# Revit family: SIMES_S.5402W_Minilinear-Miniround
name_source: partatom
category: Lighting Fixtures
revit_build: Autodesk Revit 2016 (Build: 20150714_1515(x64)
units: mm (PartAtom-declared; Revit-internal decimal feet)

## family parameters
Cut with Voids When Loaded = No
Host = Face
Light Source = Yes
OmniClass Number = 23.80.70.14
OmniClass Title = Luminaries for External Lighting
Part Type = Normal
Room Calculation Point = No
Round Connector Dimension = Use Diameter
Shared = No

## types (1)
- SIMES_S.5402W_Minilinear-Miniround
    Approval mark = CE
    Assembly Code = D5020
    BIMobject category = Outside
    BIMobject category code = lighting-outside
    BIMobject main category = Lighting
    BIMobject main category code = lighting
    Brand url = http://www.simes.it
    Color Filter = 16777215
    Color Rendering Index = CRI 90
    Colour Temperature = 3000
    Control Gear = electronic transformer
    Default Elevation = 1219 mm
    Description = MINIROUND FULL GLASS
Art. S.5402W
MODULES LED 3000K  230V CRI 90 MacAdam step 3
Rated luminaire luminous flux: 392lm
Rated input power: 10.7W
Luminaire efficacy: 37lm/W
Electronic ballast 220÷240V 50/60Hz
CE

PRODUCT TYPE
Inground walk over fitting. Recessing depth 95 mm. IP rating IP 67
MATERIAL CHARACTERISTICS
"Copper Free" Aluminium die cast housing in EN AB-44100 with high resistance against corrosion. Stone wash surface treatment prior to painting process. A4 grade Stainless Steel screws with 2,5-3% molybdenum content which increases the resistance against corrosion. Pre treated Silicone Gaskets (Minilinear). Painting Process : 3 Step Process
1) Surface treatment with BONDERITE. A heavy metal free chemical surface treatment containing ceramic nano particles giving a cohesive, inorganic and highly dense protective coating. 2) PRE POLYMERIZATION a process of introducing an epoxy primer with excellent characteristics to the paint which also offers very high resistance to oxidation due to its Zinc content. 3) POLYMERIZATION a process with the application of polyester powder with high resistance against UV rays and harsh weather conditions. Resistance test protection for Marine applications for 1200h.  Mechanical resistance IK 09 Maximum load capacity 500 Kg
LIGHTING PERFORMANCE
 acid-etched  Toughened glass 6mm thick. Lamp  fixed position. LOR -- Compact electronic ballast to guarantee better lamp stability, lifetime and reduced energy consumption.
LOW SURFACE TEMPERATURE
Surface temperature of glass 40°C (Ta 25°C) Electronic Ballast generating less heat. 
Specific layout of internal components allow for better heat dissipation therefore limiting the temperature generated inside the fitting.
RECESSING BOX
Recessing box in alluminium (Minilinear) or polypropylene (Miniround)with cable entry on all 4 sides also allows: 1) Easy wiring; 2) Cable management for fast connector; 3) Easy access to the fitting for maintenance purposes.
WIRING
Supply 0.5m cable section type H07RN-F and sealed with B component epoxy resin, wired internally protected by silicon sheaths. Fast connector M20 (Ø 5÷14 mm) supplied as standard for single cable connection . Connector housed inside the recessing box . Connection joint: The housing of Miniround has a 'dove-tail' joint to perfectly connect two or more consecutive fittings  (5 consecutive products create a full circle). Isolation: CLASS I . Finishing : FULL-GLASS Weight: 2.7 Kg Glow Wire test: --
L.E.D circuit included.
This luminaire contains built-in LED modules with energy class: A, A+, A++. In case of damage or malfunction please contact the manufacturer to receive additional instructions on how to replace and relative spare parts to order. The LED modules cannot be handled in the luminaire by the end user (Regulation UE 874/2012).
LED circuit boards are engineered accordingly to actual Lumen Maintenance regulation (LM80) and Technical Memorandum (TM21) where uniformity and quality of light is 50.000 hours referred to L70  B20 Ta 25°C.Lifecycle refers to LED circuit boards only, all others components of the luminaire are excluded.
    Design country = Italy
    Dimming Lamp Color Temperature Shift = <None>
    Edition number = 1
    Frequency = 50/60Hz
    IFC Classification = Light Fixture
    IK Rating = IK 08
    Installation instructions = http://www.simes.it
    Lamp = LED
    Lamp Light Flux = 958
    Lamp Power = 12
    Lamp count = 1
    Last Update = 08/11/2018 11:49:34
    Lifetime = 50000 L70 B20 Ta 25°C
    Light Output Ratio = 100
    Luminous efficacy = 36,6
    Manufacturer = SIMES
    Manufacturer country = Italy
    Manufacturer name = Simes
    Masterformat 2014 Code = 26 56 00
    Masterformat 2014 Description = Exterior Lighting
    Material main = Glass
    Material secondary = Aluminium
    Model = S.5402W
    Mounting Place = Floor
    Mounting Type = Recessed
    NBS Reference Code = 49
    NBS Reference Description = Luminaries And Lamps
    Nominal height = 0
    Nominal width = 0
    OmniClass Code = 23-35 47 11
    OmniClass Description = Lighting Fixture
    Photometric Web File = S5402W.ies
    Product Group = floor-recessed luminaires
    Product Guid = 3cf145a8-e862-4d30-a363-8b9dfffab22c
    Product Name = Minilinear-Miniround
    Product SKU = MINILINEAR-MINIROUND
    Product certification = http://www.simes.it
    Product data url = https://bimobject.com
    Product family = Walk over
    Product url = http://www.simes.it
    Protection Class = Protection class I
    Protection Degree = IP 67
    QR code = http://bimobject.com
    System Light Flux = 392
    System Power = 10,7
    Technical description = http://www.simes.it
    Tilt Angle = 90.00°
    Type Comments = SIMES S.p.A. - All rights reserved
    Type Image = miniround_tuttovetro_acidato.jpg
    UNSPSC Code = 3911
    URL = http://www.simes.it
    Uniclass 1.4 Code = YJ73
    Uniclass 1.4 Description = Luminaries and lamps
    Uniclass 2.0 Code = PR-49
    Uniclass 2.0 Description = Luminaries and lamps
    Uniclass 2015 Code = EF_70_80
    Uniclass 2015 Name = Lighting
    Uniformat II Code = D5020
    Uniformat II Description = Lighting & Branch Wiring
    Voltage = 220÷240V
    Wattage Comments = 11.0W
    Weight Net (Kg) = 0

## geometry (parser evidence)
native form markers: Blend x2
no freeform markers — native parametric forms only
